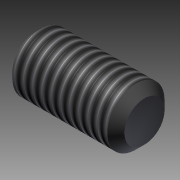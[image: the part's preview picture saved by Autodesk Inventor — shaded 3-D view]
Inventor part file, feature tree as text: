
AUTODESK INVENTOR PART (.ipt)
format: ipt  version: 2011 SP1 (Build 150282100, 282)  size: 117,248 bytes
history: native  units: mm
features: other x7, sketch x3, revolve x2, thread x1, extrude x1
ambient origin geometry x8: Origin, YZ Plane, XZ Plane, XY Plane, X Axis, Y Axis, Z Axis, Center Point
bodies: Solid1 (feature_tree)
feature tree (14):
  revolve  "Revolution1"  [1 undecoded]
  thread  "Thread1"  [1 undecoded]
  extrude  "Extrusion1"  TaperAngle=0.0deg  [1 undecoded]
  revolve  "Revolution2"  [1 undecoded]
  other  "CP_XY"
  other  "CP_YZ"
  other  "CP_ZX"
  other  "CP_X"
  other  "CP_Y"
  other  "CP_Z"
  other  "CP_Center"
  sketch  "Sketch_1"  dims[d0=360.0deg d1=8.2595mm d2=0.0mm d3=2.0mm d4=0.0mm]
  sketch  "Sketch_2"  dims[d5=360.0deg d6=0.0mm]
  sketch  "Sketch_3"
note: 4 required parameter values undecoded (feature->parameter linkage not recoverable at this tier; creation-order binding heuristic only, values carry confidence <= 0.55)